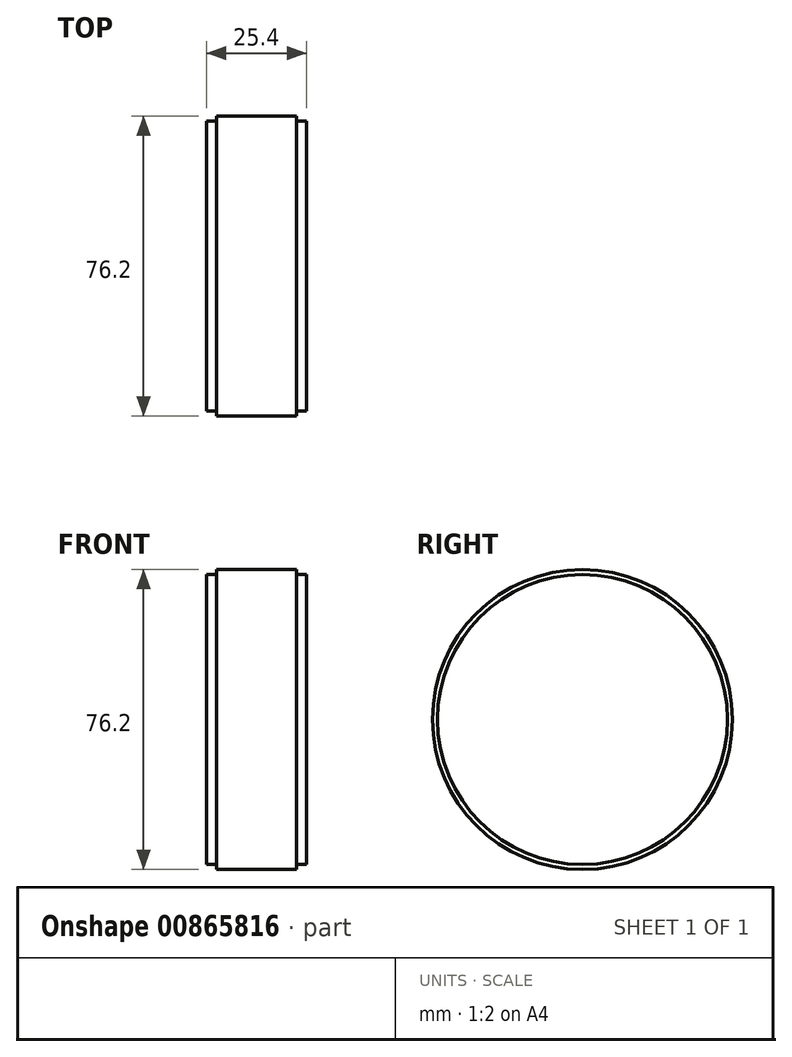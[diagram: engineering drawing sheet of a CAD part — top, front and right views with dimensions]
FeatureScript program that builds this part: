
annotation { "Feature Type Name" : "Feature", "Feature Type Description" : "" }
export const myFeature = defineFeature(function(context is Context, id is Id, definition is map)
    precondition{}
    {
        {
            var Q0;
            Q0=qCreatedBy(makeId("Right.planeOp"),FACE);
            var sketch = newSketch(context, id + "F0", { "sketchPlane" : qUnion([Q0])});
            skCircle(sketch, "E0", {"center": v(0, 0) * mm, "radius": 36.83 * mm});
            skSolve(sketch);
        }
        {
            var Q0;
            Q0=makeQuery(id+"F0.imprint","IMPRINT",FACE,{"disambiguationData":[TD([[makeQuery(id+"F0.imprint","IMPRINT",EDGE,{"derivedFrom":sQuery(id+"F0.wireOp",EDGE,"E0")}),1.0]])]});
            extrude(context, id + "F1", {"entities" : qUnion([Q0]), "oppositeDirection" : true, "depth" : 2.54 * mm, "offsetDistance" : 25.4 * mm});
        }
        {
            var Q0;
            Q0=makeQuery(id+"F1.opExtrude","CAP_FACE",FACE,{"disambiguationData":[OSD([sQuery(id+"F0.wireOp",EDGE,"E0")])],"isStart":true});
            var sketch = newSketch(context, id + "F2", { "sketchPlane" : qUnion([Q0])});
            skCircle(sketch, "E1", {"center": v(0, 0) * mm, "radius": 38.1 * mm});
            skSolve(sketch);
        }
        {
            var Q0;
            Q0=makeQuery(id+"F2.imprint","IMPRINT",FACE,{"disambiguationData":[TD([[makeQuery(id+"F2.imprint","IMPRINT",EDGE,{"derivedFrom":makeQuery(id+"F1.opExtrude","CAP_EDGE",EDGE,{"disambiguationData":[OSD([sQuery(id+"F0.wireOp",EDGE,"E0")])],"isStart":false})}),1.0]])]});
            var Q1;
            Q1=makeQuery(id+"F2.imprint","IMPRINT",FACE,{"disambiguationData":[TD([[makeQuery(id+"F2.imprint","IMPRINT",EDGE,{"derivedFrom":makeQuery(id+"F1.opExtrude","CAP_EDGE",EDGE,{"disambiguationData":[OSD([sQuery(id+"F0.wireOp",EDGE,"E0")])],"isStart":true})}),1.0]])]});
            var Q2;
            Q2=makeQuery(id+"F2.imprint","IMPRINT",FACE,{"disambiguationData":[TD([[makeQuery(id+"F2.imprint","IMPRINT",EDGE,{"derivedFrom":sQuery(id+"F2.wireOp",EDGE,"E1")}),1.0]])]});
            extrude(context, id + "F3", {"entities" : qUnion([Q0, Q1, Q2]), "operationType" : NewBodyOperationType.ADD, "depth" : 20.32 * mm, "offsetDistance" : 25.4 * mm});
        }
        {
            var Q0;
            Q0=makeQuery(id+"F3.opExtrude","CAP_FACE",FACE,{"disambiguationData":[OSD([sQuery(id+"F2.wireOp",EDGE,"E1")])],"isStart":false});
            var sketch = newSketch(context, id + "F4", { "sketchPlane" : qUnion([Q0])});
            skCircle(sketch, "E2", {"center": v(0, 0) * mm, "radius": 36.83 * mm});
            skSolve(sketch);
        }
        {
            var Q0;
            Q0=makeQuery(id+"F4.imprint","IMPRINT",FACE,{"disambiguationData":[TD([[makeQuery(id+"F4.imprint","IMPRINT",EDGE,{"derivedFrom":sQuery(id+"F4.wireOp",EDGE,"E2")}),1.0]])]});
            extrude(context, id + "F5", {"entities" : qUnion([Q0]), "operationType" : NewBodyOperationType.ADD, "depth" : 2.54 * mm, "offsetDistance" : 25.4 * mm});
        }
    });
